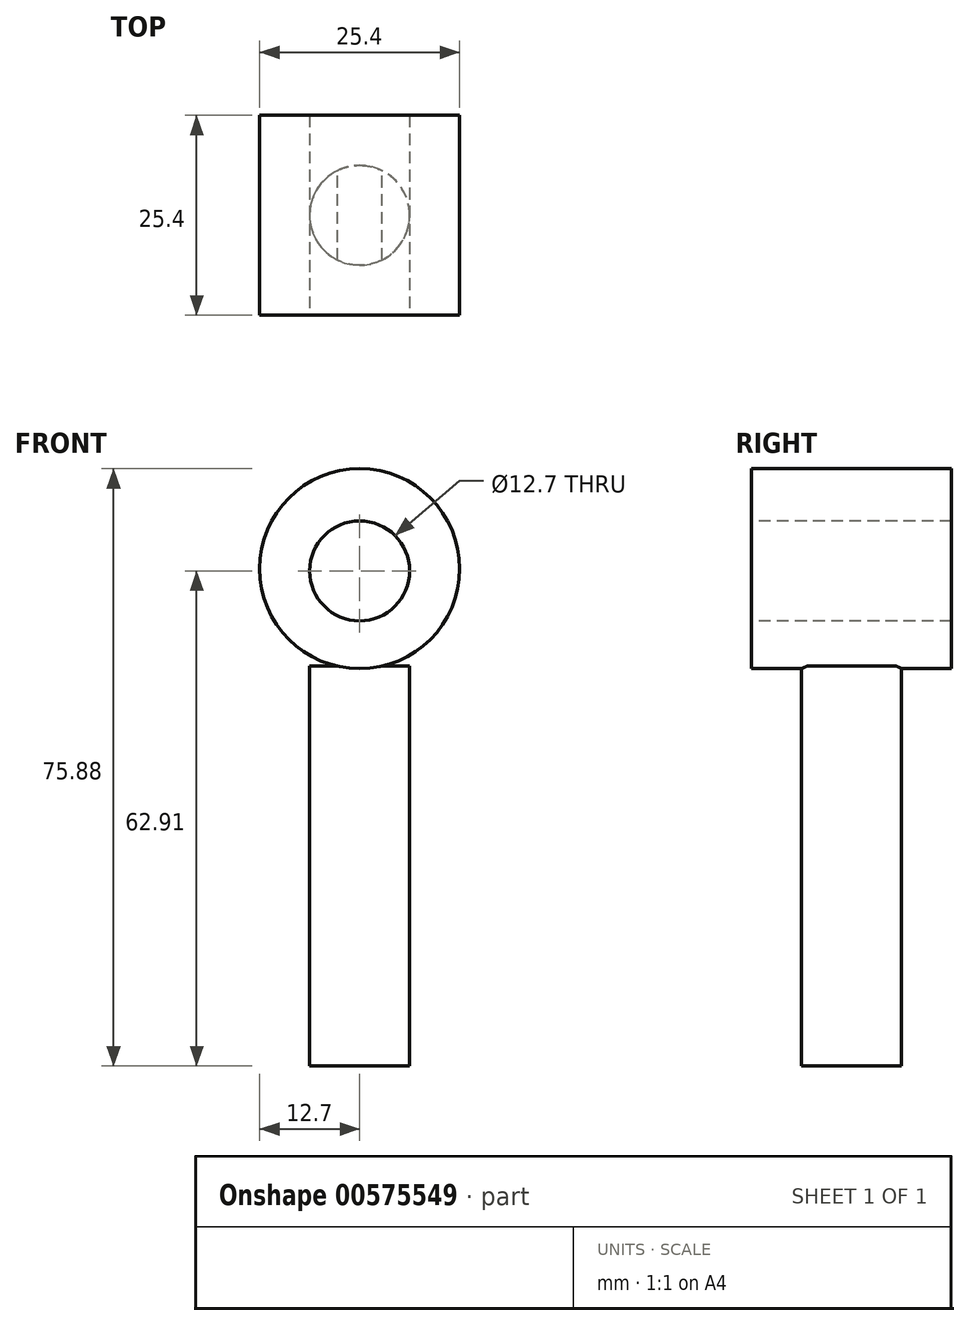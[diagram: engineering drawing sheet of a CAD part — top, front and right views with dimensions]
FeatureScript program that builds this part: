
annotation { "Feature Type Name" : "Feature", "Feature Type Description" : "" }
export const myFeature = defineFeature(function(context is Context, id is Id, definition is map)
    precondition{}
    {
        {
            var Q0;
            Q0=qCreatedBy(makeId("Top.planeOp"),FACE);
            var sketch = newSketch(context, id + "F0", { "sketchPlane" : qUnion([Q0])});
            skCircle(sketch, "E0", {"center": v(0, 0) * mm, "radius": 6.35 * mm});
            skSolve(sketch);
        }
        {
            var Q0;
            Q0=makeQuery(id+"F0.imprint","IMPRINT",FACE,{"disambiguationData":[TD([[makeQuery(id+"F0.imprint","IMPRINT",EDGE,{"derivedFrom":sQuery(id+"F0.wireOp",EDGE,"E0")}),1.0]])]});
            extrude(context, id + "F1", {"entities" : qUnion([Q0]), "depth" : -50.8 * mm, "offsetDistance" : 25.4 * mm});
        }
        {
            var Q0;
            Q0=qCreatedBy(makeId("Front.planeOp"),FACE);
            var sketch = newSketch(context, id + "F2", { "sketchPlane" : qUnion([Q0])});
            skCircle(sketch, "E1", {"center": v(0, 12.38) * mm, "radius": 12.7 * mm});
            skSolve(sketch);
        }
        {
            var Q0;
            Q0=makeQuery(id+"F2.imprint","IMPRINT",FACE,{"disambiguationData":[TD([[makeQuery(id+"F2.imprint","IMPRINT",EDGE,{"derivedFrom":sQuery(id+"F2.wireOp",EDGE,"E1")}),1.0]])]});
            extrude(context, id + "F3", {"entities" : qUnion([Q0]), "operationType" : NewBodyOperationType.ADD, "endBound" : BoundingType.SYMMETRIC, "depth" : 25.4 * mm, "offsetDistance" : 25.4 * mm});
        }
        {
            var Q0;
            Q0=qCreatedBy(makeId("Front.planeOp"),FACE);
            var sketch = newSketch(context, id + "F4", { "sketchPlane" : qUnion([Q0])});
            skCircle(sketch, "E2", {"center": v(0, 12.11) * mm, "radius": 6.35 * mm});
            skSolve(sketch);
        }
        {
            var Q0;
            Q0 = qSketchRegion(id + "F4", true);
            extrude(context, id + "F5", {"entities" : qUnion([Q0]), "operationType" : NewBodyOperationType.REMOVE, "endBound" : BoundingType.SYMMETRIC, "oppositeDirection" : true, "depth" : 25.4 * mm, "offsetDistance" : 25.4 * mm});
        }
    });
